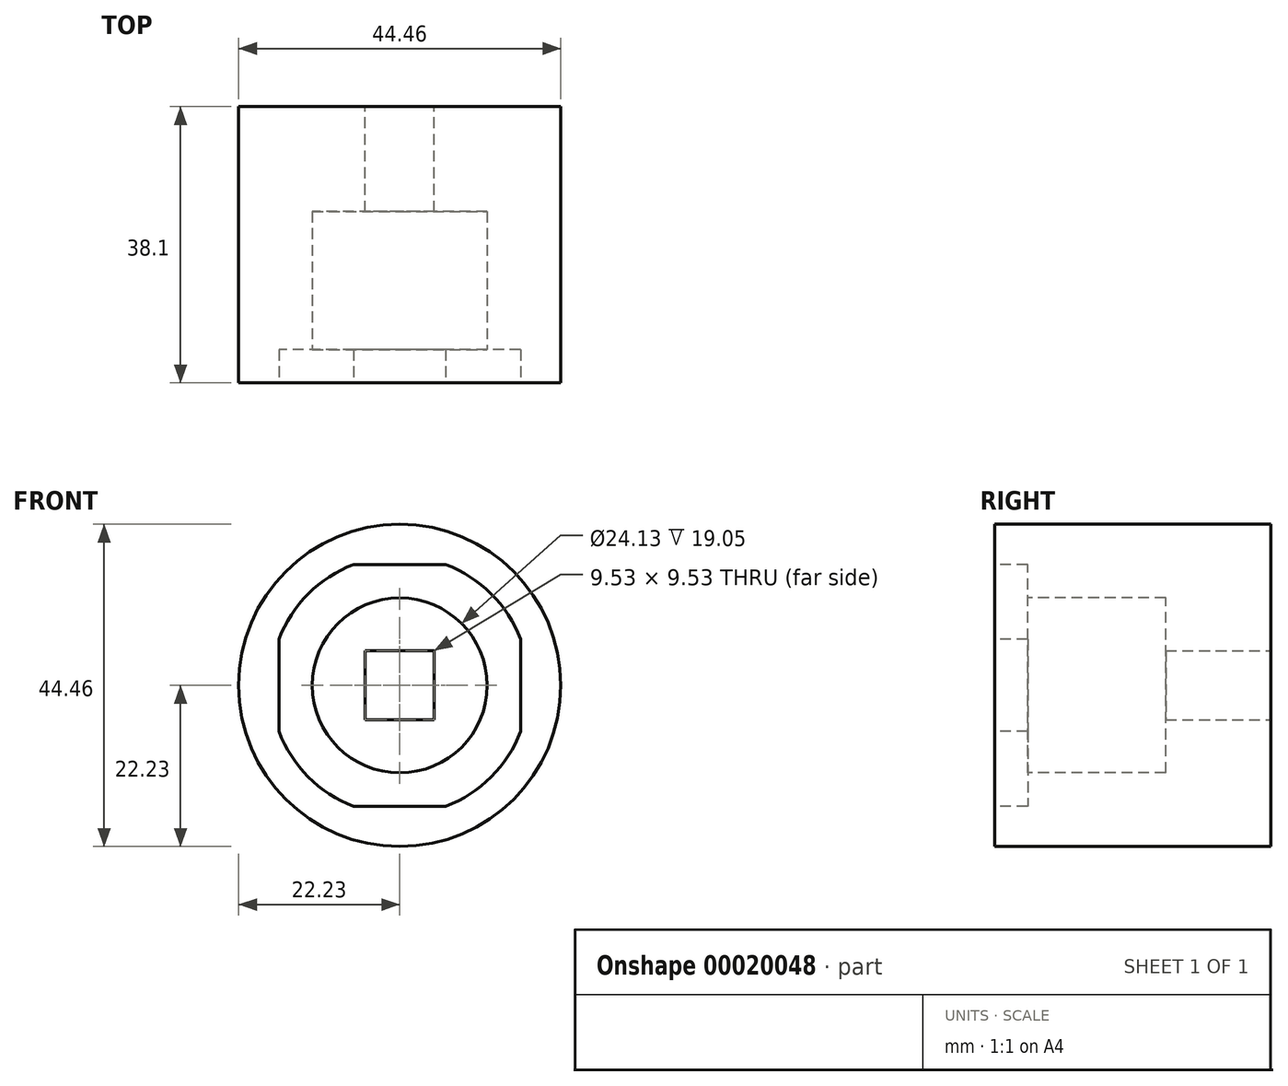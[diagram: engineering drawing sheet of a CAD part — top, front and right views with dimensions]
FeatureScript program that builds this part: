
annotation { "Feature Type Name" : "Feature", "Feature Type Description" : "" }
export const myFeature = defineFeature(function(context is Context, id is Id, definition is map)
    precondition{}
    {
        {
            var Q0;
            Q0=qCreatedBy(makeId("Front.planeOp"),FACE);
            var sketch = newSketch(context, id + "F0", { "sketchPlane" : qUnion([Q0])});
            skCircle(sketch, "E0", {"center": v(0, 0) * mm, "radius": 22.23 * mm});
            skSolve(sketch);
        }
        {
            var Q0;
            Q0 = qSketchRegion(id + "F0", true);
            extrude(context, id + "F1", {"entities" : qUnion([Q0]), "oppositeDirection" : true, "depth" : 38.1 * mm});
        }
        {
            var Q0;
            Q0=makeQuery(id+"F1.opExtrude","CAP_FACE",FACE,{"disambiguationData":[OSD([sQuery(id+"F0.wireOp",EDGE,"E0")])],"isStart":true});
            var sketch = newSketch(context, id + "F2", { "sketchPlane" : qUnion([Q0])});
            skArc(sketch, "E1", {"start": v(-6.35, 16.68) * mm, "mid": v(-12.62, 12.62) * mm, "end": v(-16.68, 6.35) * mm});
            skLineSegment(sketch, "E2.rect.bottom", {"start": v(6.35, 16.68) * mm, "end": v(-6.35, 16.68) * mm});
            skLineSegment(sketch, "E2.rect.top", {"start": v(6.35, -16.68) * mm, "end": v(-6.35, -16.68) * mm});
            skLineSegment(sketch, "E2.rect.left", {"start": v(16.68, 6.35) * mm, "end": v(16.68, -6.35) * mm});
            skLineSegment(sketch, "E2.rect.right", {"start": v(-16.68, 6.35) * mm, "end": v(-16.68, -6.35) * mm});
            skPoint(sketch, "E3.orphan", {"position": v(-16.68, 16.68) * mm});
            skPoint(sketch, "E4.orphan", {"position": v(16.68, 16.68) * mm});
            skArc(sketch, "E5.trimOffspring", {"start": v(16.68, 6.35) * mm, "mid": v(12.62, 12.62) * mm, "end": v(6.35, 16.68) * mm});
            skPoint(sketch, "E6.orphan", {"position": v(16.68, -16.68) * mm});
            skArc(sketch, "E7.trimOffspring", {"start": v(6.35, -16.68) * mm, "mid": v(12.62, -12.62) * mm, "end": v(16.68, -6.35) * mm});
            skPoint(sketch, "E8.orphan", {"position": v(-16.68, -16.68) * mm});
            skArc(sketch, "E9.trimOffspring", {"start": v(-16.68, -6.35) * mm, "mid": v(-12.62, -12.62) * mm, "end": v(-6.35, -16.68) * mm});
            skSolve(sketch);
        }
        {
            var Q0;
            Q0 = qSketchRegion(id + "F2", true);
            extrude(context, id + "F3", {"entities" : qUnion([Q0]), "operationType" : NewBodyOperationType.REMOVE, "oppositeDirection" : true, "depth" : 4.57 * mm});
        }
        {
            var Q0;
            Q0=makeQuery(id+"F3.boolean.opBoolean","COPY",FACE,{"derivedFrom":makeQuery(id+"F3.opExtrude","CAP_FACE",FACE,{"disambiguationData":[OSD([sQuery(id+"F2.wireOp",EDGE,"E1"),sQuery(id+"F2.wireOp",EDGE,"E2.rect.bottom"),sQuery(id+"F2.wireOp",EDGE,"E2.rect.top"),sQuery(id+"F2.wireOp",EDGE,"E2.rect.left"),sQuery(id+"F2.wireOp",EDGE,"E2.rect.right"),sQuery(id+"F2.wireOp",EDGE,"E5.trimOffspring"),sQuery(id+"F2.wireOp",EDGE,"E7.trimOffspring"),sQuery(id+"F2.wireOp",EDGE,"E9.trimOffspring")])],"isStart":false})});
            var sketch = newSketch(context, id + "F4", { "sketchPlane" : qUnion([Q0])});
            skCircle(sketch, "E10", {"center": v(0, 0) * mm, "radius": 12.06 * mm});
            skSolve(sketch);
        }
        {
            var Q0;
            Q0 = qSketchRegion(id + "F4", true);
            extrude(context, id + "F5", {"entities" : qUnion([Q0]), "operationType" : NewBodyOperationType.REMOVE, "oppositeDirection" : true, "depth" : 19.05 * mm});
        }
        {
            var Q0;
            Q0=makeQuery(id+"F1.opExtrude","CAP_FACE",FACE,{"disambiguationData":[OSD([sQuery(id+"F0.wireOp",EDGE,"E0")])],"isStart":false});
            var sketch = newSketch(context, id + "F6", { "sketchPlane" : qUnion([Q0])});
            skLineSegment(sketch, "E11.rect.bottom", {"start": v(-4.76, 4.76) * mm, "end": v(4.76, 4.76) * mm});
            skLineSegment(sketch, "E11.rect.top", {"start": v(-4.76, -4.76) * mm, "end": v(4.76, -4.76) * mm});
            skLineSegment(sketch, "E11.rect.left", {"start": v(-4.76, 4.76) * mm, "end": v(-4.76, -4.76) * mm});
            skLineSegment(sketch, "E11.rect.right", {"start": v(4.76, 4.76) * mm, "end": v(4.76, -4.76) * mm});
            skPoint(sketch, "E11.rect.middle", {"position": v(0, 0) * mm});
            skSolve(sketch);
        }
        {
            var Q0;
            Q0 = qSketchRegion(id + "F6", true);
            extrude(context, id + "F7", {"entities" : qUnion([Q0]), "operationType" : NewBodyOperationType.REMOVE, "endBound" : BoundingType.UP_TO_NEXT, "oppositeDirection" : true, "depth" : 25.4 * mm});
        }
    });
